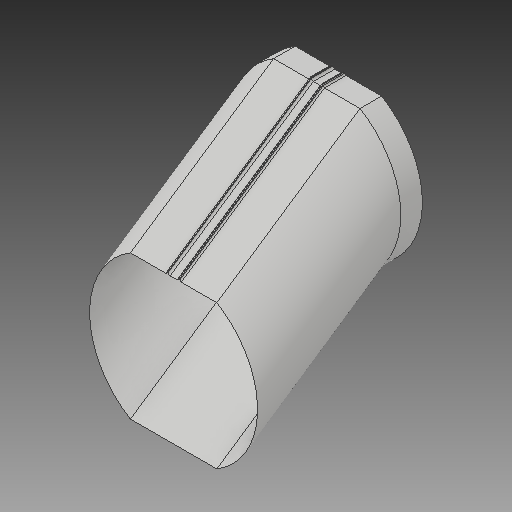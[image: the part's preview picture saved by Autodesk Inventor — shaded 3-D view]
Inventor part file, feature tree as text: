
AUTODESK INVENTOR PART (.ipt)
format: ipt  version: 2017 (Build 210142000, 142)  size: 170,496 bytes
history: native  units: in
note: dims shown in document units (in); Inventor stores cm internally (conversion verified against a paired STEP export)
features: sketch x2, extrude x1, plane x1, sweep x1, delete_face x1
ambient origin geometry x8: Origin, YZ Plane, XZ Plane, XY Plane, X Axis, Y Axis, Z Axis, Center Point
bodies: Solid1 (feature_tree)
feature tree (6):
  sketch  "Sketch1"  dims[d0=6.6667in d3=1.0in d4=0.0in d12=8.0in]
  extrude  "connecction top"  Depth=6.6667in
  plane  "Work Plane2"
  sweep  "ramp"
  delete_face  "Delete Face1"
  sketch  "Sketch6"  dims[d28=8.0in d45=0.0in d46=0.0in d65=0.8521in d66=4.0in d67=0.5833in d68=3.8873in d69=3.8873in d70=1.7083in d71=0.0625in d72=0.0625in d73=1.6458in d74=0.25in d75=0.125in d77=0.0884in d78=45.0deg d79=3.3333in d80=0.125in]
